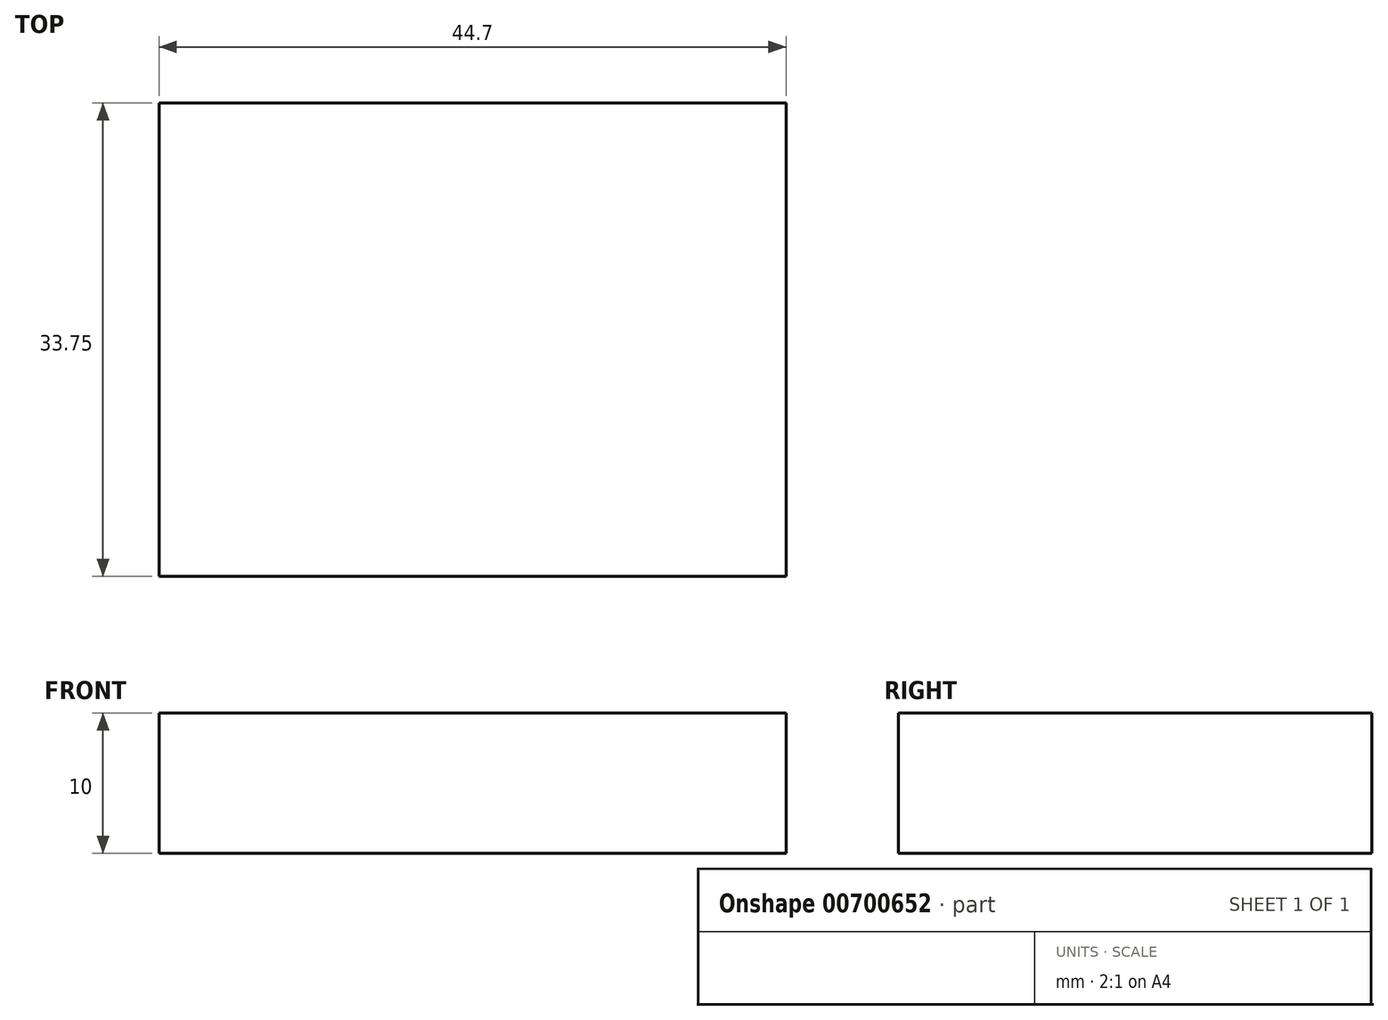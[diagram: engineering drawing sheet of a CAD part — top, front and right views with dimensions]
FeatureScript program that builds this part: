
annotation { "Feature Type Name" : "Feature", "Feature Type Description" : "" }
export const myFeature = defineFeature(function(context is Context, id is Id, definition is map)
    precondition{}
    {
        {
            var Q0;
            Q0=qCreatedBy(makeId("Top.planeOp"),FACE);
            var sketch = newSketch(context, id + "F0", { "sketchPlane" : qUnion([Q0])});
            skLineSegment(sketch, "E0.bottom", {"start": v(-19.87, 15.15) * mm, "end": v(24.83, 15.15) * mm});
            skLineSegment(sketch, "E0.top", {"start": v(-19.87, -18.6) * mm, "end": v(24.83, -18.6) * mm});
            skLineSegment(sketch, "E0.left", {"start": v(-19.87, 15.15) * mm, "end": v(-19.87, -18.6) * mm});
            skLineSegment(sketch, "E0.right", {"start": v(24.83, 15.15) * mm, "end": v(24.83, -18.6) * mm});
            skSolve(sketch);
        }
        {
            var Q0;
            Q0=makeQuery(id+"F0.imprint","IMPRINT",FACE,{"disambiguationData":[TD([[makeQuery(id+"F0.imprint","IMPRINT",EDGE,{"derivedFrom":sQuery(id+"F0.wireOp",EDGE,"E0.bottom")}),-1.0]])]});
            extrude(context, id + "F1", {"entities" : qUnion([Q0]), "depth" : 10 * mm, "offsetDistance" : 25.4 * mm});
        }
    });
